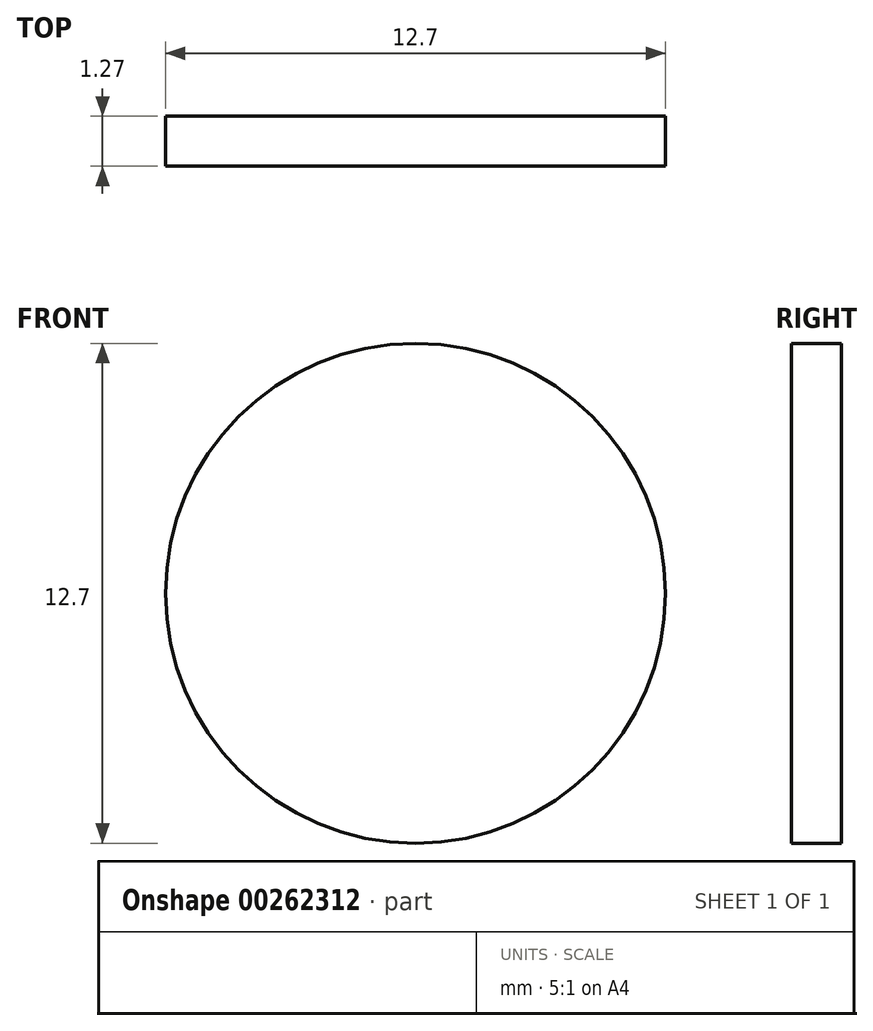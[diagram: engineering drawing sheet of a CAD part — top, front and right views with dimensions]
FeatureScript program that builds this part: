
annotation { "Feature Type Name" : "Feature", "Feature Type Description" : "" }
export const myFeature = defineFeature(function(context is Context, id is Id, definition is map)
    precondition{}
    {
        {
            var Q0;
            Q0=qCreatedBy(makeId("Front.planeOp"),FACE);
            var sketch = newSketch(context, id + "F0", { "sketchPlane" : qUnion([Q0])});
            skCircle(sketch, "E0", {"center": v(0, 0) * mm, "radius": 6.35 * mm});
            skSolve(sketch);
        }
        {
            var Q0;
            Q0=makeQuery(id+"F0.imprint","IMPRINT",FACE,{"disambiguationData":[TD([[makeQuery(id+"F0.imprint","IMPRINT",EDGE,{"derivedFrom":sQuery(id+"F0.wireOp",EDGE,"E0")}),1.0]])]});
            extrude(context, id + "F1", {"entities" : qUnion([Q0]), "depth" : 1.27 * mm});
        }
    });
